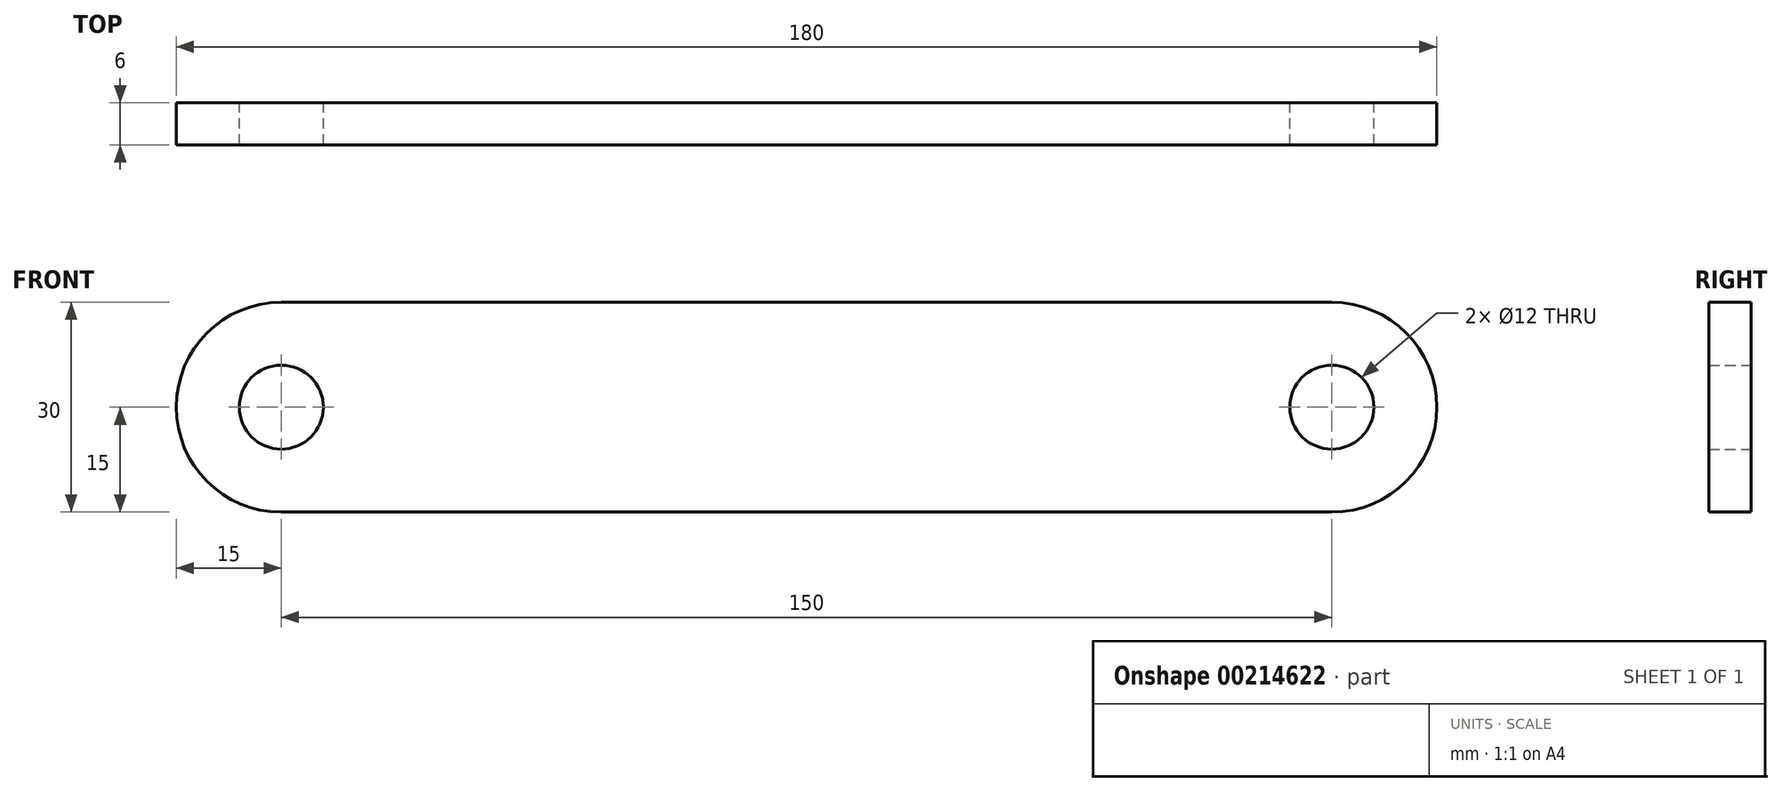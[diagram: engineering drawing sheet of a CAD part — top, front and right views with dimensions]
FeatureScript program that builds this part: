
annotation { "Feature Type Name" : "Feature", "Feature Type Description" : "" }
export const myFeature = defineFeature(function(context is Context, id is Id, definition is map)
    precondition{}
    {
        {
            var Q0;
            Q0=qCreatedBy(makeId("Front.planeOp"),FACE);
            var sketch = newSketch(context, id + "F0", { "sketchPlane" : qUnion([Q0])});
            skCircle(sketch, "E0", {"center": v(0, 0) * mm, "radius": 6 * mm});
            skCircle(sketch, "E1", {"center": v(150, 0) * mm, "radius": 6 * mm});
            skArc(sketch, "E2", {"start": v(0, 15) * mm, "mid": v(-15, 0) * mm, "end": v(0, -15) * mm});
            skArc(sketch, "E3", {"start": v(150, -15) * mm, "mid": v(165, 0) * mm, "end": v(150, 15) * mm});
            skLineSegment(sketch, "E4", {"start": v(0, 15) * mm, "end": v(150, 15) * mm});
            skLineSegment(sketch, "E5", {"start": v(150, -15) * mm, "end": v(0, -15) * mm});
            skSolve(sketch);
        }
        {
            var Q0;
            Q0=makeQuery(id+"F0.imprint","IMPRINT",FACE,{"disambiguationData":[TD([[makeQuery(id+"F0.imprint","IMPRINT",EDGE,{"derivedFrom":sQuery(id+"F0.wireOp",EDGE,"E0")}),-1.0]])]});
            extrude(context, id + "F1", {"entities" : qUnion([Q0]), "depth" : 6 * mm});
        }
    });
